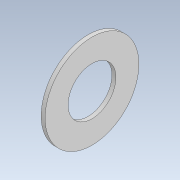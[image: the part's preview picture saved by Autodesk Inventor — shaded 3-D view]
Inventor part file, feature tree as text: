
AUTODESK INVENTOR PART (.ipt)
format: ipt  version: 2021 (Build 250183000, 183)  size: 83,456 bytes
history: native  units: mm
features: other x1, extrude x1, sketch x1
ambient origin geometry x8: Origin, YZ Plane, XZ Plane, XY Plane, X Axis, Y Axis, Z Axis, Center Point
bodies: Body1 (feature_tree)
feature tree (3):
  other  "Sólido1"
  extrude  "Extrusión1"  [1 undecoded]
  sketch  "Boceto1"  dims[d3=0.0mm]
note: 1 required parameter value undecoded (feature->parameter linkage not recoverable at this tier; creation-order binding heuristic only, values carry confidence <= 0.55)
